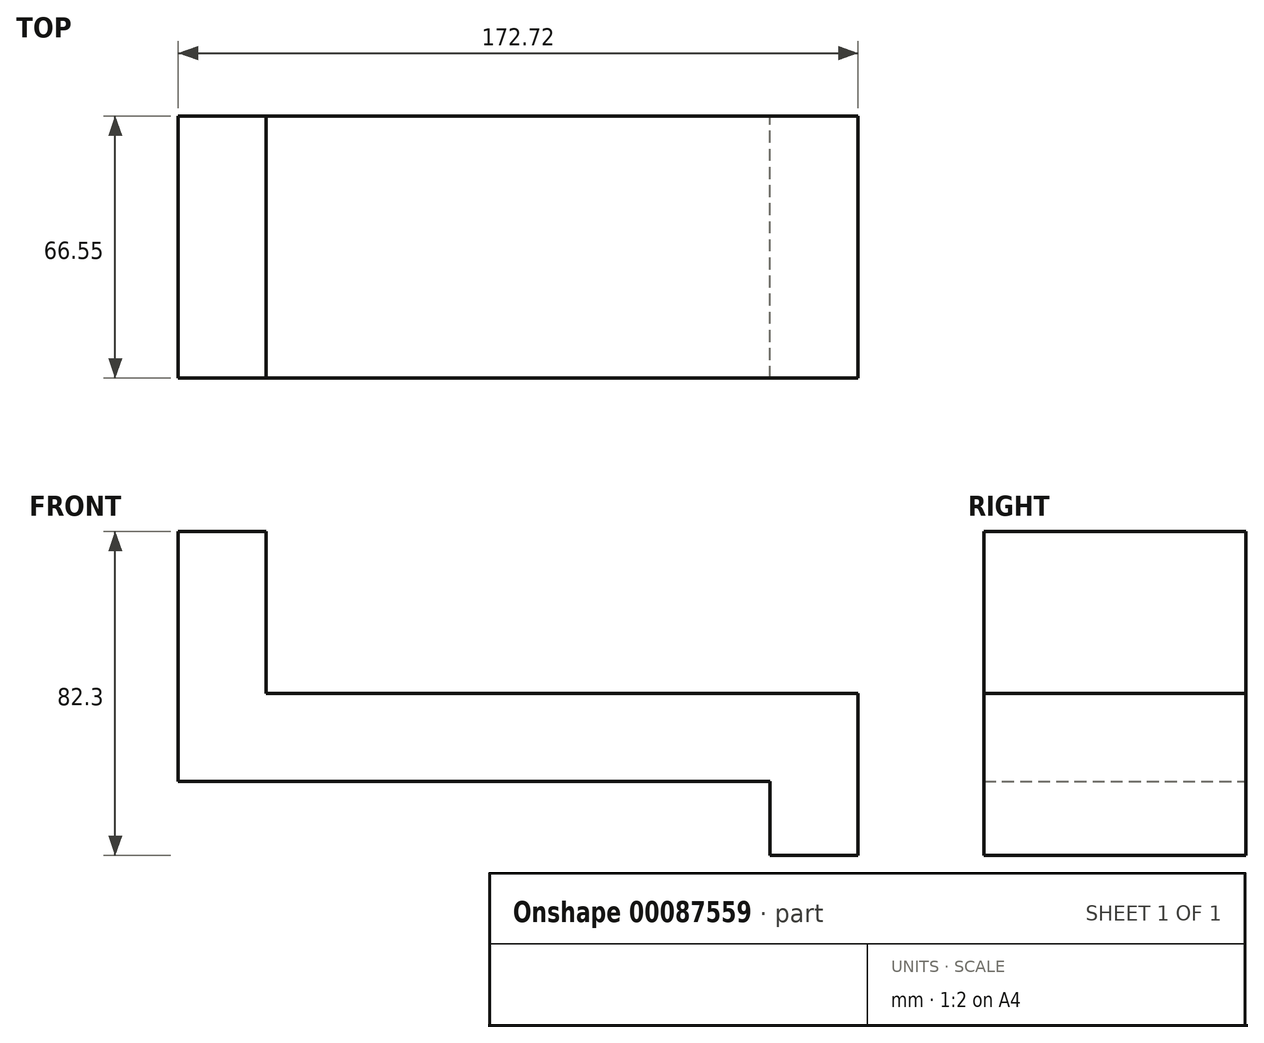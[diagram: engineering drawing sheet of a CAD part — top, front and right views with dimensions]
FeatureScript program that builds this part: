
annotation { "Feature Type Name" : "Feature", "Feature Type Description" : "" }
export const myFeature = defineFeature(function(context is Context, id is Id, definition is map)
    precondition{}
    {
        {
            var Q0;
            Q0=qCreatedBy(makeId("Front.planeOp"),FACE);
            var sketch = newSketch(context, id + "F0", { "sketchPlane" : qUnion([Q0])});
            skLineSegment(sketch, "E0", {"start": v(0, 0) * mm, "end": v(150.37, 0) * mm});
            skLineSegment(sketch, "E1", {"start": v(150.37, 0) * mm, "end": v(150.37, -18.8) * mm});
            skLineSegment(sketch, "E2", {"start": v(150.37, -18.8) * mm, "end": v(172.72, -18.8) * mm});
            skLineSegment(sketch, "E3", {"start": v(172.72, -18.8) * mm, "end": v(172.72, 22.35) * mm});
            skLineSegment(sketch, "E4", {"start": v(172.72, 22.35) * mm, "end": v(22.35, 22.35) * mm});
            skLineSegment(sketch, "E5", {"start": v(22.35, 22.35) * mm, "end": v(22.35, 63.5) * mm});
            skLineSegment(sketch, "E6", {"start": v(22.35, 63.5) * mm, "end": v(0, 63.5) * mm});
            skLineSegment(sketch, "E7", {"start": v(0, 63.5) * mm, "end": v(0, 0) * mm});
            skSolve(sketch);
        }
        {
            var Q0;
            Q0=makeQuery(id+"F0.imprint","IMPRINT",FACE,{"disambiguationData":[TD([[makeQuery(id+"F0.imprint","IMPRINT",EDGE,{"derivedFrom":sQuery(id+"F0.wireOp",EDGE,"E0")}),1.0]])]});
            extrude(context, id + "F1", {"entities" : qUnion([Q0]), "depth" : 66.55 * mm});
        }
    });
